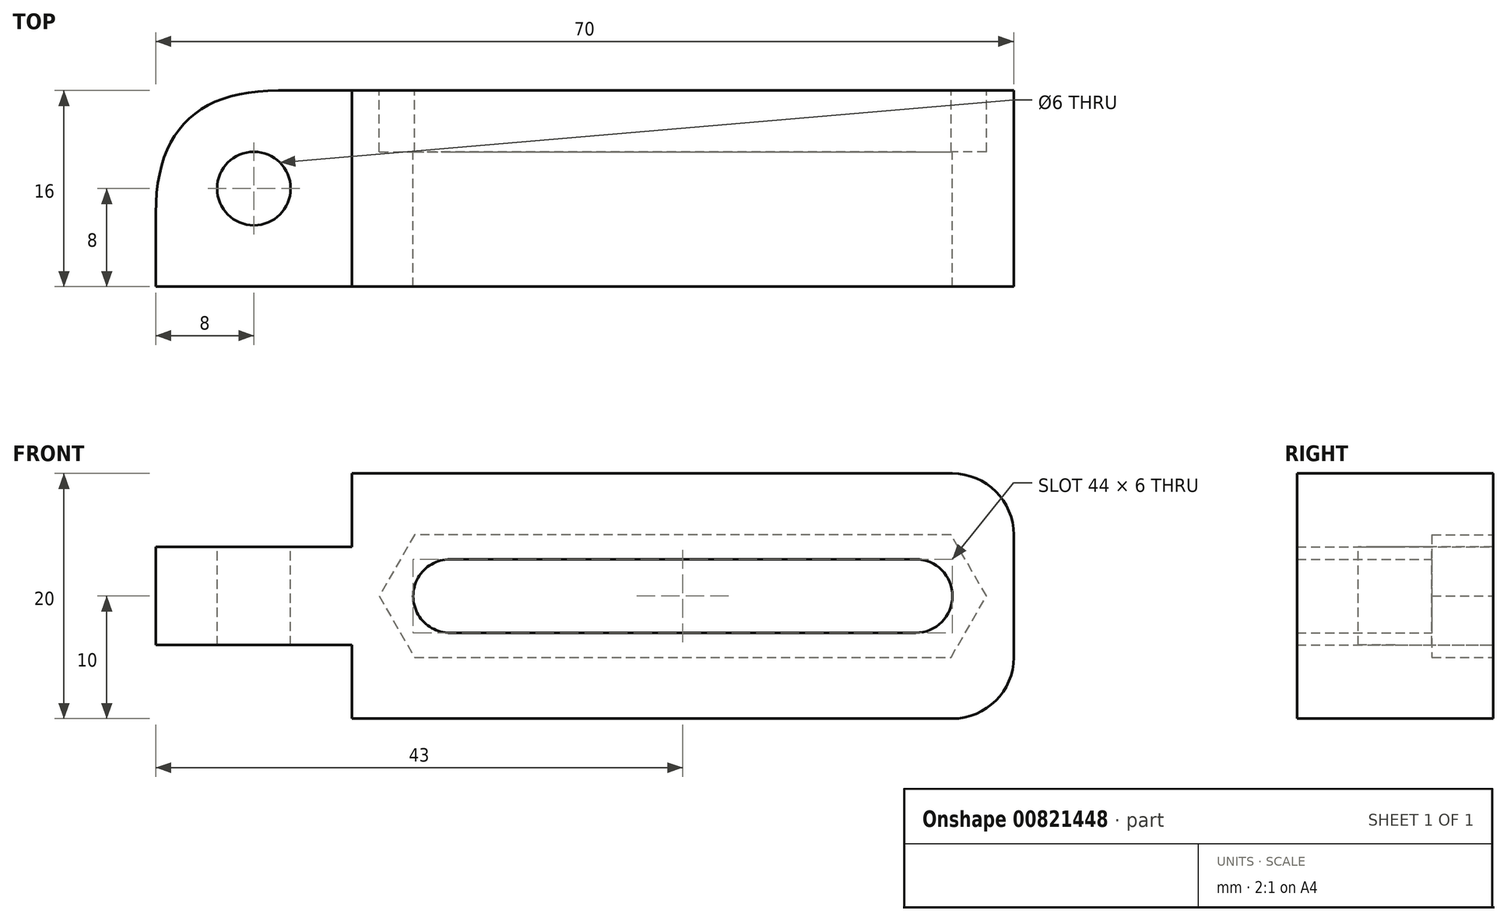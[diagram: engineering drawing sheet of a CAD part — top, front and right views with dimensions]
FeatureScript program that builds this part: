
annotation { "Feature Type Name" : "Feature", "Feature Type Description" : "" }
export const myFeature = defineFeature(function(context is Context, id is Id, definition is map)
    precondition{}
    {
        {
            var Q0;
            Q0=qCreatedBy(makeId("Top.planeOp"),FACE);
            var sketch = newSketch(context, id + "F0", { "sketchPlane" : qUnion([Q0])});
            skLineSegment(sketch, "E0.bottom", {"start": v(35, -8) * mm, "end": v(-35, -8) * mm});
            skLineSegment(sketch, "E0.top", {"start": v(35, 8) * mm, "end": v(-35, 8) * mm});
            skLineSegment(sketch, "E0.left", {"start": v(35, -8) * mm, "end": v(35, 8) * mm});
            skLineSegment(sketch, "E0.right", {"start": v(-35, -8) * mm, "end": v(-35, 8) * mm});
            skPoint(sketch, "E0.middle", {"position": v(0, 0) * mm});
            skSolve(sketch);
        }
        {
            var Q0;
            Q0 = qSketchRegion(id + "F0", true);
            extrude(context, id + "F1", {"entities" : qUnion([Q0]), "depth" : 20 * mm, "offsetDistance" : 25 * mm});
        }
        {
            var Q0;
            Q0=makeQuery(id+"F1.opExtrude","CAP_FACE",FACE,{"disambiguationData":[OSD([sQuery(id+"F0.wireOp",EDGE,"E0.bottom"),sQuery(id+"F0.wireOp",EDGE,"E0.top"),sQuery(id+"F0.wireOp",EDGE,"E0.left"),sQuery(id+"F0.wireOp",EDGE,"E0.right")])],"isStart":false});
            var sketch = newSketch(context, id + "F2", { "sketchPlane" : qUnion([Q0])});
            skLineSegment(sketch, "E1.bottom", {"start": v(-35, -8) * mm, "end": v(-19, -8) * mm});
            skLineSegment(sketch, "E1.top", {"start": v(-35, 8) * mm, "end": v(-19, 8) * mm});
            skLineSegment(sketch, "E1.left", {"start": v(-35, -8) * mm, "end": v(-35, 8) * mm});
            skLineSegment(sketch, "E1.right", {"start": v(-19, -8) * mm, "end": v(-19, 8) * mm});
            skSolve(sketch);
        }
        {
            var Q0;
            Q0 = qSketchRegion(id + "F2", true);
            extrude(context, id + "F3", {"entities" : qUnion([Q0]), "operationType" : NewBodyOperationType.REMOVE, "oppositeDirection" : true, "depth" : 6 * mm, "offsetDistance" : 25 * mm});
        }
        {
            var Q0;
            Q0=makeQuery(id+"F1.opExtrude","CAP_FACE",FACE,{"disambiguationData":[OSD([sQuery(id+"F0.wireOp",EDGE,"E0.bottom"),sQuery(id+"F0.wireOp",EDGE,"E0.top"),sQuery(id+"F0.wireOp",EDGE,"E0.left"),sQuery(id+"F0.wireOp",EDGE,"E0.right")])],"isStart":true});
            var sketch = newSketch(context, id + "F4", { "sketchPlane" : qUnion([Q0])});
            skLineSegment(sketch, "E2.bottom", {"start": v(-35, 8) * mm, "end": v(-19, 8) * mm});
            skLineSegment(sketch, "E2.top", {"start": v(-35, -8) * mm, "end": v(-19, -8) * mm});
            skLineSegment(sketch, "E2.left", {"start": v(-35, 8) * mm, "end": v(-35, -8) * mm});
            skLineSegment(sketch, "E2.right", {"start": v(-19, 8) * mm, "end": v(-19, -8) * mm});
            skSolve(sketch);
        }
        {
            var Q0;
            Q0 = qSketchRegion(id + "F4", true);
            extrude(context, id + "F5", {"entities" : qUnion([Q0]), "operationType" : NewBodyOperationType.REMOVE, "oppositeDirection" : true, "depth" : 6 * mm, "offsetDistance" : 25 * mm});
        }
        {
            var Q0;
            Q0=makeQuery(id+"F3.boolean.opBoolean","COPY",FACE,{"derivedFrom":makeQuery(id+"F3.opExtrude","CAP_FACE",FACE,{"disambiguationData":[OSD([sQuery(id+"F2.wireOp",EDGE,"E1.bottom"),sQuery(id+"F2.wireOp",EDGE,"E1.top"),sQuery(id+"F2.wireOp",EDGE,"E1.left"),sQuery(id+"F2.wireOp",EDGE,"E1.right")])],"isStart":false})});
            var sketch = newSketch(context, id + "F6", { "sketchPlane" : qUnion([Q0])});
            skCircle(sketch, "E3", {"center": v(-27, 0) * mm, "radius": 3 * mm});
            skSolve(sketch);
        }
        {
            var Q0;
            Q0 = qSketchRegion(id + "F6", true);
            extrude(context, id + "F7", {"entities" : qUnion([Q0]), "operationType" : NewBodyOperationType.REMOVE, "oppositeDirection" : true, "depth" : 25 * mm, "offsetDistance" : 25 * mm});
        }
        {
            var Q0;
            Q0=makeQuery(id+"F1.opExtrude","SWEPT_EDGE",EDGE,{"disambiguationData":[OSD([sQuery(id+"F0.wireOp",EDGE,"E0.top"),sQuery(id+"F0.wireOp",EDGE,"E0.right")])]});
            fillet(context, id + "F8", {"entities" : qUnion([Q0]), "radius" : 10 * mm, "tangentPropagation" : true, "rho" : 0.5, "crossSection" : FilletCrossSection.CONIC, "allowEdgeOverflow" : false});
        }
        {
            var Q0;
            Q0=makeQuery(id+"F1.opExtrude","SWEPT_FACE",FACE,{"disambiguationData":[OSD([sQuery(id+"F0.wireOp",EDGE,"E0.top")])]});
            var sketch = newSketch(context, id + "F9", { "sketchPlane" : qUnion([Q0])});
            skCircle(sketch, "E4.cCircle", {"center": v(-27, 10) * mm, "radius": 5 * mm, "construction": true});
            skPoint(sketch, "E4.cCircle.centerSnap0", {"position": v(-35, 10) * mm});
            skLineSegment(sketch, "E4.0", {"start": v(-24.11, 5) * mm, "end": v(-29.89, 5) * mm});
            skLineSegment(sketch, "E4.1", {"start": v(-29.89, 5) * mm, "end": v(-32.77, 10) * mm});
            skLineSegment(sketch, "E4.2", {"start": v(-32.77, 10) * mm, "end": v(-29.89, 15) * mm});
            skLineSegment(sketch, "E4.3", {"start": v(-29.89, 15) * mm, "end": v(-24.11, 15) * mm});
            skLineSegment(sketch, "E4.4", {"start": v(-24.11, 15) * mm, "end": v(-21.23, 10) * mm});
            skLineSegment(sketch, "E4.5", {"start": v(-21.23, 10) * mm, "end": v(-24.11, 5) * mm});
            skPoint(sketch, "E4.0.midPoint", {"position": v(-27, 5) * mm});
            skCircle(sketch, "E5.cCircle", {"center": v(11, 10) * mm, "radius": 5 * mm, "construction": true});
            skLineSegment(sketch, "E5.0", {"start": v(8.11, 15) * mm, "end": v(13.89, 15) * mm});
            skLineSegment(sketch, "E5.1", {"start": v(13.89, 15) * mm, "end": v(16.77, 10) * mm});
            skLineSegment(sketch, "E5.2", {"start": v(16.77, 10) * mm, "end": v(13.89, 5) * mm});
            skLineSegment(sketch, "E5.3", {"start": v(13.89, 5) * mm, "end": v(8.11, 5) * mm});
            skLineSegment(sketch, "E5.4", {"start": v(8.11, 5) * mm, "end": v(5.23, 10) * mm});
            skLineSegment(sketch, "E5.5", {"start": v(5.23, 10) * mm, "end": v(8.11, 15) * mm});
            skPoint(sketch, "E5.0.midPoint", {"position": v(11, 15) * mm});
            skLineSegment(sketch, "E6", {"start": v(8.11, 5) * mm, "end": v(-24.11, 5) * mm});
            skLineSegment(sketch, "E7", {"start": v(-24.11, 15) * mm, "end": v(8.11, 15) * mm});
            skSolve(sketch);
        }
        {
            var Q0;
            Q0 = qSketchRegion(id + "F9", true);
            extrude(context, id + "F10", {"entities" : qUnion([Q0]), "operationType" : NewBodyOperationType.REMOVE, "oppositeDirection" : true, "depth" : 5 * mm, "offsetDistance" : 25 * mm});
        }
        {
            var Q0;
            Q0=makeQuery(id+"F10.boolean.opBoolean","COPY",FACE,{"derivedFrom":makeQuery(id+"F10.opExtrude","CAP_FACE",FACE,{"disambiguationData":[OSD([sQuery(id+"F9.wireOp",EDGE,"E4.0"),sQuery(id+"F9.wireOp",EDGE,"E4.1"),sQuery(id+"F9.wireOp",EDGE,"E4.2"),sQuery(id+"F9.wireOp",EDGE,"E4.3"),sQuery(id+"F9.wireOp",EDGE,"E5.0"),sQuery(id+"F9.wireOp",EDGE,"E5.1"),sQuery(id+"F9.wireOp",EDGE,"E5.2"),sQuery(id+"F9.wireOp",EDGE,"E5.3"),sQuery(id+"F9.wireOp",EDGE,"E6"),sQuery(id+"F9.wireOp",EDGE,"E7")])],"isStart":false})});
            var sketch = newSketch(context, id + "F11", { "sketchPlane" : qUnion([Q0])});
            skCircle(sketch, "E8", {"center": v(-27, 10) * mm, "radius": 3 * mm});
            skCircle(sketch, "E9", {"center": v(11, 10) * mm, "radius": 3 * mm});
            skLineSegment(sketch, "E10", {"start": v(11.03, 7) * mm, "end": v(-27, 7) * mm});
            skLineSegment(sketch, "E11", {"start": v(-27, 7) * mm, "end": v(-27, 13) * mm});
            skLineSegment(sketch, "E12", {"start": v(-27, 13) * mm, "end": v(11, 13) * mm});
            skLineSegment(sketch, "E13", {"start": v(11, 13) * mm, "end": v(11.03, 7) * mm});
            skSolve(sketch);
        }
        {
            var Q0;
            Q0 = qSketchRegion(id + "F11", true);
            extrude(context, id + "F12", {"entities" : qUnion([Q0]), "operationType" : NewBodyOperationType.REMOVE, "endBound" : BoundingType.UP_TO_NEXT, "oppositeDirection" : true, "depth" : 25 * mm, "offsetDistance" : 25 * mm});
        }
        {
            var Q0;
            Q0=makeQuery(id+"F1.opExtrude","CAP_EDGE",EDGE,{"disambiguationData":[OSD([sQuery(id+"F0.wireOp",EDGE,"E0.left")])],"isStart":false});
            var Q1;
            Q1=makeQuery(id+"F1.opExtrude","CAP_EDGE",EDGE,{"disambiguationData":[OSD([sQuery(id+"F0.wireOp",EDGE,"E0.left")])],"isStart":true});
            fillet(context, id + "F13", {"entities" : qUnion([Q0, Q1]), "radius" : 5 * mm, "tangentPropagation" : true, "allowEdgeOverflow" : false});
        }
    });
